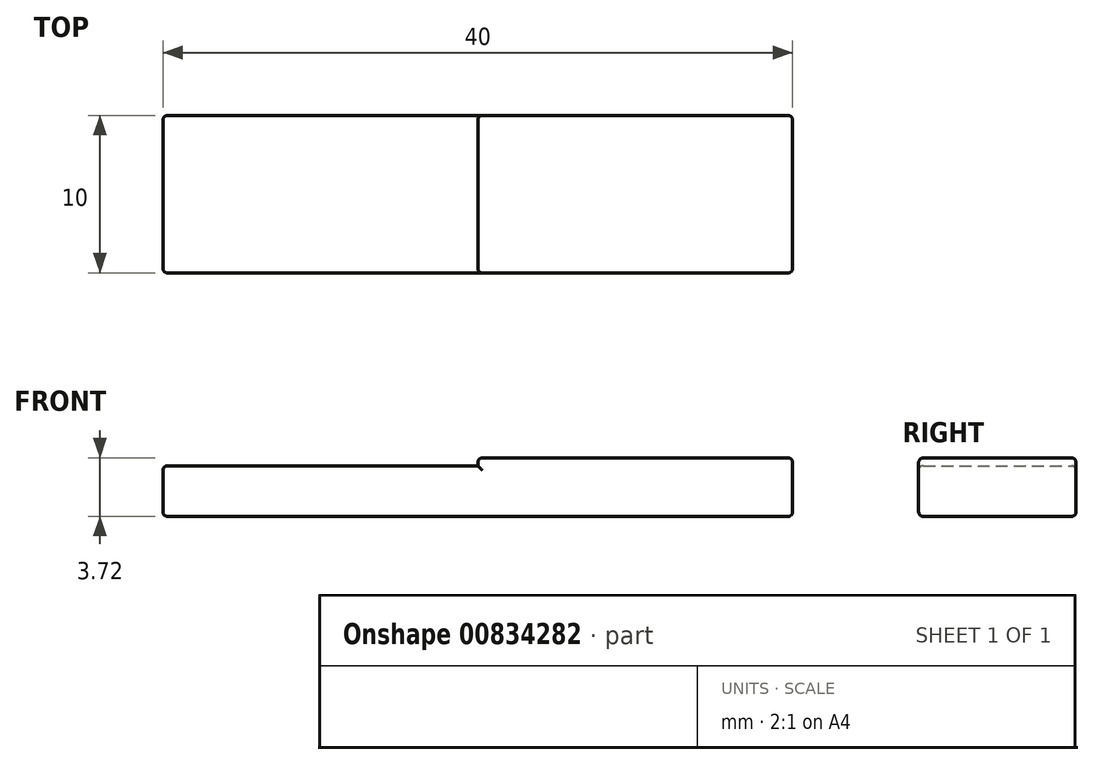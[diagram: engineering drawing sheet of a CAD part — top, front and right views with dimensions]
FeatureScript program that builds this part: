
annotation { "Feature Type Name" : "Feature", "Feature Type Description" : "" }
export const myFeature = defineFeature(function(context is Context, id is Id, definition is map)
    precondition{}
    {
        {
            var Q0;
            Q0=qCreatedBy(makeId("Front.planeOp"),FACE);
            var sketch = newSketch(context, id + "F0", { "sketchPlane" : qUnion([Q0])});
            skLineSegment(sketch, "E0", {"start": v(0, 0) * mm, "end": v(40, 0) * mm});
            skLineSegment(sketch, "E1", {"start": v(40, 0) * mm, "end": v(40, 3.72) * mm});
            skLineSegment(sketch, "E2", {"start": v(40, 3.72) * mm, "end": v(20, 3.72) * mm});
            skLineSegment(sketch, "E3", {"start": v(20, 3.72) * mm, "end": v(20, 3.22) * mm});
            skLineSegment(sketch, "E4", {"start": v(20, 3.22) * mm, "end": v(0, 3.22) * mm});
            skLineSegment(sketch, "E5", {"start": v(0, 3.22) * mm, "end": v(0, 0) * mm});
            skSolve(sketch);
        }
        {
            var Q0;
            Q0=makeQuery(id+"F0.imprint","IMPRINT",FACE,{"disambiguationData":[TD([[makeQuery(id+"F0.imprint","IMPRINT",EDGE,{"derivedFrom":sQuery(id+"F0.wireOp",EDGE,"E0")}),1.0]])]});
            extrude(context, id + "F1", {"entities" : qUnion([Q0]), "endBound" : BoundingType.SYMMETRIC, "depth" : 10 * mm, "offsetDistance" : 25.4 * mm});
        }
        {
            var Q0;
            Q0=makeQuery(id+"F1.opExtrude","CAP_EDGE",EDGE,{"disambiguationData":[OSD([sQuery(id+"F0.wireOp",EDGE,"E2")])],"isStart":true});
            var Q1;
            Q1=makeQuery(id+"F1.opExtrude","CAP_EDGE",EDGE,{"disambiguationData":[OSD([sQuery(id+"F0.wireOp",EDGE,"E1")])],"isStart":true});
            var Q2;
            Q2=makeQuery(id+"F1.opExtrude","CAP_EDGE",EDGE,{"disambiguationData":[OSD([sQuery(id+"F0.wireOp",EDGE,"E0")])],"isStart":true});
            var Q3;
            Q3=makeQuery(id+"F1.opExtrude","SWEPT_EDGE",EDGE,{"disambiguationData":[OSD([sQuery(id+"F0.wireOp",EDGE,"E2"),sQuery(id+"F0.wireOp",EDGE,"E3")])]});
            var Q4;
            Q4=makeQuery(id+"F1.opExtrude","CAP_EDGE",EDGE,{"disambiguationData":[OSD([sQuery(id+"F0.wireOp",EDGE,"E4")])],"isStart":true});
            var Q5;
            Q5=makeQuery(id+"F1.opExtrude","CAP_EDGE",EDGE,{"disambiguationData":[OSD([sQuery(id+"F0.wireOp",EDGE,"E3")])],"isStart":true});
            var Q6;
            Q6=makeQuery(id+"F1.opExtrude","CAP_EDGE",EDGE,{"disambiguationData":[OSD([sQuery(id+"F0.wireOp",EDGE,"E5")])],"isStart":true});
            var Q7;
            Q7=makeQuery(id+"F1.opExtrude","SWEPT_EDGE",EDGE,{"disambiguationData":[OSD([sQuery(id+"F0.wireOp",EDGE,"E4"),sQuery(id+"F0.wireOp",EDGE,"E5")])]});
            var Q8;
            Q8=makeQuery(id+"F1.opExtrude","SWEPT_EDGE",EDGE,{"disambiguationData":[OSD([sQuery(id+"F0.wireOp",EDGE,"E0"),sQuery(id+"F0.wireOp",EDGE,"E5")])]});
            var Q9;
            Q9=makeQuery(id+"F1.opExtrude","CAP_EDGE",EDGE,{"disambiguationData":[OSD([sQuery(id+"F0.wireOp",EDGE,"E5")])],"isStart":false});
            var Q10;
            Q10=makeQuery(id+"F1.opExtrude","CAP_EDGE",EDGE,{"disambiguationData":[OSD([sQuery(id+"F0.wireOp",EDGE,"E4")])],"isStart":false});
            var Q11;
            Q11=makeQuery(id+"F1.opExtrude","CAP_EDGE",EDGE,{"disambiguationData":[OSD([sQuery(id+"F0.wireOp",EDGE,"E2")])],"isStart":false});
            var Q12;
            Q12=makeQuery(id+"F1.opExtrude","SWEPT_EDGE",EDGE,{"disambiguationData":[OSD([sQuery(id+"F0.wireOp",EDGE,"E1"),sQuery(id+"F0.wireOp",EDGE,"E2")])]});
            var Q13;
            Q13=makeQuery(id+"F1.opExtrude","CAP_EDGE",EDGE,{"disambiguationData":[OSD([sQuery(id+"F0.wireOp",EDGE,"E0")])],"isStart":false});
            var Q14;
            Q14=makeQuery(id+"F1.opExtrude","CAP_EDGE",EDGE,{"disambiguationData":[OSD([sQuery(id+"F0.wireOp",EDGE,"E1")])],"isStart":false});
            var Q15;
            Q15=makeQuery(id+"F1.opExtrude","SWEPT_EDGE",EDGE,{"disambiguationData":[OSD([sQuery(id+"F0.wireOp",EDGE,"E0"),sQuery(id+"F0.wireOp",EDGE,"E1")])]});
            var Q16;
            Q16=makeQuery(id+"F1.opExtrude","CAP_EDGE",EDGE,{"disambiguationData":[OSD([sQuery(id+"F0.wireOp",EDGE,"E3")])],"isStart":false});
            fillet(context, id + "F2", {"entities" : qUnion([Q0, Q1, Q2, Q3, Q4, Q5, Q6, Q7, Q8, Q9, Q10, Q11, Q12, Q13, Q14, Q15, Q16]), "radius" : .3 * mm, "tangentPropagation" : true, "allowEdgeOverflow" : false});
        }
    });
